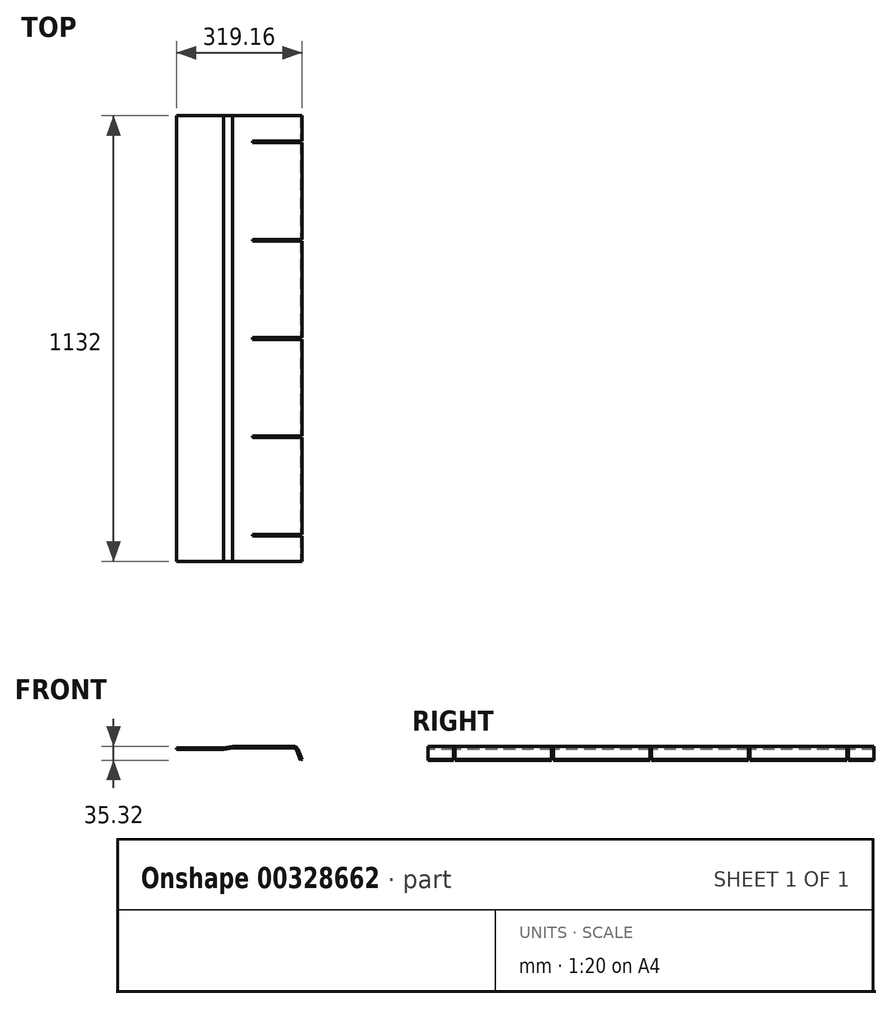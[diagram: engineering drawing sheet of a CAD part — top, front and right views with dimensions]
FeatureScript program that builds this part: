
annotation { "Feature Type Name" : "Feature", "Feature Type Description" : "" }
export const myFeature = defineFeature(function(context is Context, id is Id, definition is map)
    precondition{}
    {
        {
            var Q0;
            Q0=qCreatedBy(makeId("Front.planeOp"),FACE);
            var sketch = newSketch(context, id + "F0", { "sketchPlane" : qUnion([Q0])});
            skLineSegment(sketch, "E0.bottom", {"start": v(0, 0) * mm, "end": v(119.96, 0) * mm});
            skLineSegment(sketch, "E0.top", {"start": v(0, -4) * mm, "end": v(120.31, -4) * mm});
            skLineSegment(sketch, "E0.left", {"start": v(0, 0) * mm, "end": v(0, -4) * mm});
            skLineSegment(sketch, "E1", {"start": v(142.65, 4) * mm, "end": v(119.96, 0) * mm});
            skLineSegment(sketch, "E2", {"start": v(143, 0) * mm, "end": v(120.31, -4) * mm});
            skLineSegment(sketch, "E3.trimOffspring", {"start": v(143, 0) * mm, "end": v(296.48, 0) * mm});
            skLineSegment(sketch, "E4.trimOffspring", {"start": v(296.48, 4) * mm, "end": v(142.65, 4) * mm});
            skLineSegment(sketch, "E5", {"start": v(155, -4) * mm, "end": v(296.48, -4) * mm, "construction": true});
            skLineSegment(sketch, "E6", {"start": v(301.1, -7.09) * mm, "end": v(311, -31) * mm, "construction": true});
            skLineSegment(sketch, "E7", {"start": v(311, -31) * mm, "end": v(256.47, -31) * mm, "construction": true});
            skPoint(sketch, "E8.visualSharp", {"position": v(299.82, -4) * mm});
            skArc(sketch, "E8.filletArc", {"start": v(301.1, -7.09) * mm, "mid": v(299.25, -4.84) * mm, "end": v(296.48, -4) * mm, "construction": true});
            skLineSegment(sketch, "E9", {"start": v(155, -4) * mm, "end": v(155, 0) * mm, "construction": true});
            skLineSegment(sketch, "E10", {"start": v(304.8, -5.56) * mm, "end": v(315.46, -31.32) * mm});
            skLineSegment(sketch, "E11", {"start": v(311, -31) * mm, "end": v(314.7, -29.47) * mm});
            skPoint(sketch, "E12.visualSharp", {"position": v(302.49, 0) * mm});
            skArc(sketch, "E12.filletArc", {"start": v(304.8, -5.56) * mm, "mid": v(301.48, -1.52) * mm, "end": v(296.48, 0) * mm});
            skLineSegment(sketch, "E13", {"start": v(308.49, -4.03) * mm, "end": v(319.16, -29.79) * mm});
            skLineSegment(sketch, "E14", {"start": v(315.46, -31.32) * mm, "end": v(319.16, -29.79) * mm});
            skPoint(sketch, "E15.visualSharp", {"position": v(305.16, 4) * mm});
            skArc(sketch, "E15.filletArc", {"start": v(308.49, -4.03) * mm, "mid": v(303.7, 1.8) * mm, "end": v(296.48, 4) * mm});
            skSolve(sketch);
        }
        {
            var Q0;
            Q0=qSketchRegion(id+"F0",true);
            extrude(context, id + "F1", {"entities" : qUnion([Q0]), "oppositeDirection" : true, "depth" : 1132 * mm});
        }
        {
            var Q0;
            Q0=makeQuery(id+"F1.opExtrude","SWEPT_FACE",FACE,{"disambiguationData":[OSD([sQuery(id+"F0.wireOp",EDGE,"E4.trimOffspring")])]});
            var sketch = newSketch(context, id + "F2", { "sketchPlane" : qUnion([Q0])});
            skLineSegment(sketch, "E16", {"start": v(193, 64) * mm, "end": v(334.12, 64) * mm});
            skLineSegment(sketch, "E17", {"start": v(334.12, 64) * mm, "end": v(334.12, 68) * mm});
            skLineSegment(sketch, "E18", {"start": v(334.12, 68) * mm, "end": v(193, 68) * mm});
            skLineSegment(sketch, "E19", {"start": v(193, 68) * mm, "end": v(193, 64) * mm});
            skLineSegment(sketch, "E20.0.1.0", {"start": v(193, 314) * mm, "end": v(334.12, 314) * mm});
            skLineSegment(sketch, "E20.0.1.1", {"start": v(334.12, 318) * mm, "end": v(193, 318) * mm});
            skLineSegment(sketch, "E20.0.1.2", {"start": v(334.12, 314) * mm, "end": v(334.12, 318) * mm});
            skLineSegment(sketch, "E20.0.1.3", {"start": v(193, 318) * mm, "end": v(193, 314) * mm});
            skLineSegment(sketch, "E20.0.2.0", {"start": v(193, 564) * mm, "end": v(334.12, 564) * mm});
            skLineSegment(sketch, "E20.0.2.1", {"start": v(334.12, 568) * mm, "end": v(193, 568) * mm});
            skLineSegment(sketch, "E20.0.2.2", {"start": v(334.12, 564) * mm, "end": v(334.12, 568) * mm});
            skLineSegment(sketch, "E20.0.2.3", {"start": v(193, 568) * mm, "end": v(193, 564) * mm});
            skLineSegment(sketch, "E20.0.3.0", {"start": v(193, 814) * mm, "end": v(334.12, 814) * mm});
            skLineSegment(sketch, "E20.0.3.1", {"start": v(334.12, 818) * mm, "end": v(193, 818) * mm});
            skLineSegment(sketch, "E20.0.3.2", {"start": v(334.12, 814) * mm, "end": v(334.12, 818) * mm});
            skLineSegment(sketch, "E20.0.3.3", {"start": v(193, 818) * mm, "end": v(193, 814) * mm});
            skLineSegment(sketch, "E20.0.4.0", {"start": v(193, 1064) * mm, "end": v(334.12, 1064) * mm});
            skLineSegment(sketch, "E20.0.4.1", {"start": v(334.12, 1068) * mm, "end": v(193, 1068) * mm});
            skLineSegment(sketch, "E20.0.4.2", {"start": v(334.12, 1064) * mm, "end": v(334.12, 1068) * mm});
            skLineSegment(sketch, "E20.0.4.3", {"start": v(193, 1068) * mm, "end": v(193, 1064) * mm});
            skLineSegment(sketch, "E20.direction1", {"start": v(193, 64) * mm, "end": v(193, 64) * mm});
            skLineSegment(sketch, "E20.direction2", {"start": v(193, 64) * mm, "end": v(193, 314) * mm, "construction": true});
            skSolve(sketch);
        }
        {
            var Q0;
            Q0=qSketchRegion(id+"F2",true);
            extrude(context, id + "F3", {"entities" : qUnion([Q0]), "operationType" : NewBodyOperationType.REMOVE, "endBound" : BoundingType.THROUGH_ALL, "oppositeDirection" : true, "depth" : 415.63 * mm});
        }
    });
